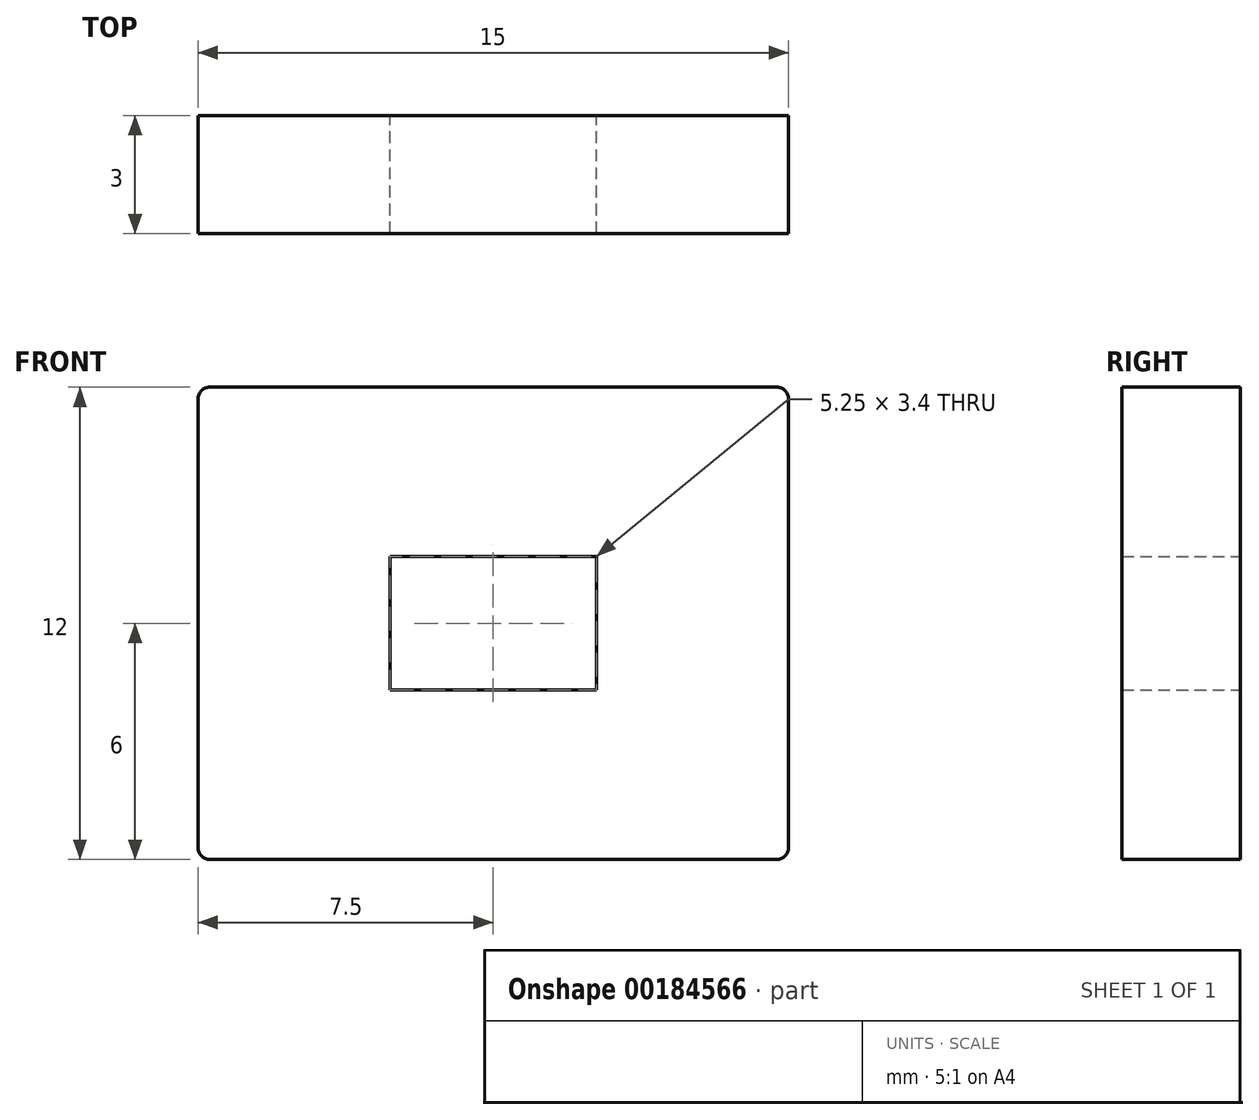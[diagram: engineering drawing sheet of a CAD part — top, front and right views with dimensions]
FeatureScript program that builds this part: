
annotation { "Feature Type Name" : "Feature", "Feature Type Description" : "" }
export const myFeature = defineFeature(function(context is Context, id is Id, definition is map)
    precondition{}
    {
        {
            var Q0;
            Q0=qCreatedBy(makeId("Front.planeOp"),FACE);
            var sketch = newSketch(context, id + "F0", { "sketchPlane" : qUnion([Q0])});
            skLineSegment(sketch, "E0.bottom", {"start": v(7.5, 6) * mm, "end": v(-7.5, 6) * mm});
            skLineSegment(sketch, "E0.top", {"start": v(7.5, -6) * mm, "end": v(-7.5, -6) * mm});
            skLineSegment(sketch, "E0.left", {"start": v(7.5, 6) * mm, "end": v(7.5, -6) * mm});
            skLineSegment(sketch, "E0.right", {"start": v(-7.5, 6) * mm, "end": v(-7.5, -6) * mm});
            skPoint(sketch, "E0.middle", {"position": v(0, 0) * mm});
            skLineSegment(sketch, "E1.bottom", {"start": v(2.63, 1.7) * mm, "end": v(-2.63, 1.7) * mm});
            skLineSegment(sketch, "E1.top", {"start": v(2.63, -1.7) * mm, "end": v(-2.63, -1.7) * mm});
            skLineSegment(sketch, "E1.left", {"start": v(2.63, 1.7) * mm, "end": v(2.63, -1.7) * mm});
            skLineSegment(sketch, "E1.right", {"start": v(-2.63, 1.7) * mm, "end": v(-2.63, -1.7) * mm});
            skSolve(sketch);
        }
        {
            var Q0;
            Q0=qSketchRegion(id+"F0",true);
            extrude(context, id + "F1", {"entities" : qUnion([Q0]), "depth" : 3 * mm});
        }
        {
            var Q0;
            Q0=makeQuery(id+"F1.opExtrude","SWEPT_EDGE",EDGE,{"disambiguationData":[OSD([sQuery(id+"F0.wireOp",EDGE,"E0.bottom"),sQuery(id+"F0.wireOp",EDGE,"E0.right")])]});
            var Q1;
            Q1=makeQuery(id+"F1.opExtrude","SWEPT_EDGE",EDGE,{"disambiguationData":[OSD([sQuery(id+"F0.wireOp",EDGE,"E0.top"),sQuery(id+"F0.wireOp",EDGE,"E0.right")])]});
            var Q2;
            Q2=makeQuery(id+"F1.opExtrude","SWEPT_EDGE",EDGE,{"disambiguationData":[OSD([sQuery(id+"F0.wireOp",EDGE,"E0.bottom"),sQuery(id+"F0.wireOp",EDGE,"E0.left")])]});
            var Q3;
            Q3=makeQuery(id+"F1.opExtrude","SWEPT_EDGE",EDGE,{"disambiguationData":[OSD([sQuery(id+"F0.wireOp",EDGE,"E0.top"),sQuery(id+"F0.wireOp",EDGE,"E0.left")])]});
            fillet(context, id + "F2", {"entities" : qUnion([Q0, Q1, Q2, Q3]), "radius" : 0.3 * mm, "tangentPropagation" : true, "allowEdgeOverflow" : false});
        }
    });
